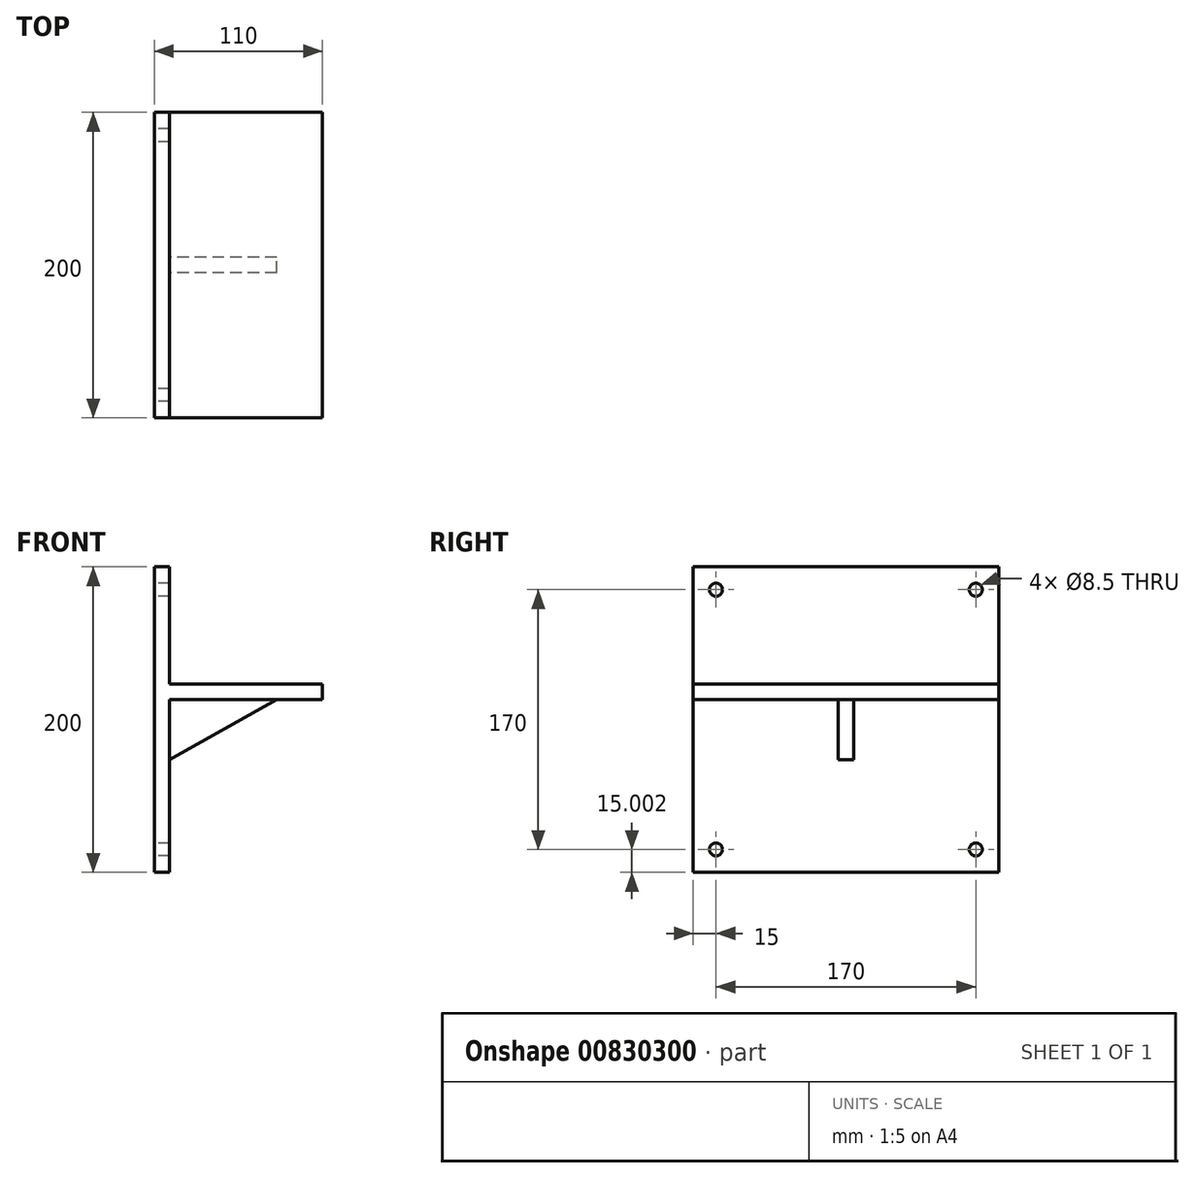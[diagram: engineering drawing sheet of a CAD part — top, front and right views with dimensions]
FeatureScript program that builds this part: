
annotation { "Feature Type Name" : "Feature", "Feature Type Description" : "" }
export const myFeature = defineFeature(function(context is Context, id is Id, definition is map)
    precondition{}
    {
        {
            var Q0;
            Q0=qCreatedBy(makeId("Front.planeOp"),FACE);
            var sketch = newSketch(context, id + "F0", { "sketchPlane" : qUnion([Q0])});
            skLineSegment(sketch, "E0", {"start": v(-54.55, 119.52) * mm, "end": v(-54.55, -80.48) * mm});
            skLineSegment(sketch, "E1", {"start": v(-54.55, -80.48) * mm, "end": v(-44.55, -80.48) * mm});
            skLineSegment(sketch, "E2", {"start": v(-44.55, -80.48) * mm, "end": v(-44.55, 32.72) * mm});
            skLineSegment(sketch, "E3", {"start": v(-44.55, 32.72) * mm, "end": v(55.45, 32.72) * mm});
            skLineSegment(sketch, "E4", {"start": v(55.45, 32.72) * mm, "end": v(55.45, 42.72) * mm});
            skLineSegment(sketch, "E5", {"start": v(55.45, 42.72) * mm, "end": v(-44.55, 42.72) * mm});
            skLineSegment(sketch, "E6", {"start": v(-44.55, 42.72) * mm, "end": v(-44.55, 119.52) * mm});
            skLineSegment(sketch, "E7", {"start": v(-54.55, 119.52) * mm, "end": v(-44.55, 119.52) * mm});
            skSolve(sketch);
        }
        {
            var Q0;
            Q0=makeQuery(id+"F0.imprint","IMPRINT",FACE,{"disambiguationData":[TD([[makeQuery(id+"F0.imprint","IMPRINT",EDGE,{"derivedFrom":sQuery(id+"F0.wireOp",EDGE,"E0")}),1.0]])]});
            extrude(context, id + "F1", {"entities" : qUnion([Q0]), "depth" : 200 * mm, "offsetDistance" : 25 * mm});
        }
        {
            var Q0;
            Q0=makeQuery(id+"F1.opExtrude","SWEPT_FACE",FACE,{"disambiguationData":[OSD([sQuery(id+"F0.wireOp",EDGE,"E2")])]});
            var sketch = newSketch(context, id + "F2", { "sketchPlane" : qUnion([Q0])});
            skLineSegment(sketch, "E8", {"start": v(-105, 32.72) * mm, "end": v(-105, -6.7) * mm});
            skLineSegment(sketch, "E9", {"start": v(-105, -6.7) * mm, "end": v(-95, -6.7) * mm});
            skLineSegment(sketch, "E10", {"start": v(-95, -6.7) * mm, "end": v(-95, 32.72) * mm});
            skLineSegment(sketch, "E11", {"start": v(-95, 32.72) * mm, "end": v(-105, 32.72) * mm});
            skSolve(sketch);
        }
        {
            var Q0;
            Q0=makeQuery(id+"F2.imprint","IMPRINT",FACE,{"disambiguationData":[TD([[makeQuery(id+"F2.imprint","IMPRINT",EDGE,{"derivedFrom":sQuery(id+"F2.wireOp",EDGE,"E8")}),1.0]])]});
            extrude(context, id + "F3", {"entities" : qUnion([Q0]), "operationType" : NewBodyOperationType.ADD, "depth" : 70 * mm, "offsetDistance" : 25 * mm});
        }
        {
            var Q0;
            Q0=makeQuery(id+"F3.opExtrude","SWEPT_FACE",FACE,{"disambiguationData":[OSD([sQuery(id+"F2.wireOp",EDGE,"E10")])]});
            var sketch = newSketch(context, id + "F4", { "sketchPlane" : qUnion([Q0])});
            skLineSegment(sketch, "E12", {"start": v(-25.45, 32.72) * mm, "end": v(44.55, -6.7) * mm});
            skSolve(sketch);
        }
        {
            var Q0;
            Q0=makeQuery(id+"F4.imprint","IMPRINT",FACE,{"disambiguationData":[TD([[makeQuery(id+"F4.imprint","IMPRINT",EDGE,{"derivedFrom":sQuery(id+"F4.wireOp",EDGE,"E12")}),-1.0]])]});
            extrude(context, id + "F5", {"entities" : qUnion([Q0]), "operationType" : NewBodyOperationType.REMOVE, "oppositeDirection" : true, "depth" : 70 * mm, "offsetDistance" : 25 * mm});
        }
        {
            var Q0;
            Q0=makeQuery(id+"F1.opExtrude","SWEPT_FACE",FACE,{"disambiguationData":[OSD([sQuery(id+"F0.wireOp",EDGE,"E0")])]});
            var sketch = newSketch(context, id + "F6", { "sketchPlane" : qUnion([Q0])});
            skLineSegment(sketch, "E13", {"start": v(15, 104.52) * mm, "end": v(185, 104.52) * mm});
            skLineSegment(sketch, "E14", {"start": v(15, 104.52) * mm, "end": v(15, -65.48) * mm});
            skLineSegment(sketch, "E15", {"start": v(15, -65.48) * mm, "end": v(185, -65.48) * mm});
            skLineSegment(sketch, "E16", {"start": v(185, 104.52) * mm, "end": v(185, -65.48) * mm});
            skCircle(sketch, "E17", {"center": v(15, 104.52) * mm, "radius": 8.5 * mm});
            skCircle(sketch, "E18", {"center": v(185, 104.52) * mm, "radius": 8.5 * mm});
            skCircle(sketch, "E19", {"center": v(185, -65.48) * mm, "radius": 8.5 * mm});
            skCircle(sketch, "E20", {"center": v(15, -65.48) * mm, "radius": 8.5 * mm});
            skSolve(sketch);
        }
        {
            var Q0;
            Q0=sQuery(id+"F6.wireOp",VERTEX,"E13.end");
            var Q1;
            Q1=sQuery(id+"F6.wireOp",VERTEX,"E13.start");
            var Q2;
            Q2=sQuery(id+"F6.wireOp",VERTEX,"E14.end");
            var Q3;
            Q3=sQuery(id+"F6.wireOp",VERTEX,"E15.end");
            var Q4;
            Q4=makeQuery(id+"F1.opExtrude","SWEPT_BODY",BODY,{"disambiguationData":[OSD([sQuery(id+"F0.wireOp",EDGE,"E0"),sQuery(id+"F0.wireOp",EDGE,"E1"),sQuery(id+"F0.wireOp",EDGE,"E2"),sQuery(id+"F0.wireOp",EDGE,"E3"),sQuery(id+"F0.wireOp",EDGE,"E4"),sQuery(id+"F0.wireOp",EDGE,"E5"),sQuery(id+"F0.wireOp",EDGE,"E6"),sQuery(id+"F0.wireOp",EDGE,"E7")])]});
            hole(context, id + "F7", {"style" : HoleStyle.SIMPLE, "endStyle" : HoleEndStyle.THROUGH, "holeDiameter" : 8.5 * mm, "majorDiameter" : 5 * mm, "isTappedThrough" : true, "tappedDepth" : 12 * mm, "tapClearance" : 3, "locations" : qUnion([Q0, Q1, Q2, Q3]), "scope" : qUnion([Q4])});
        }
    });
